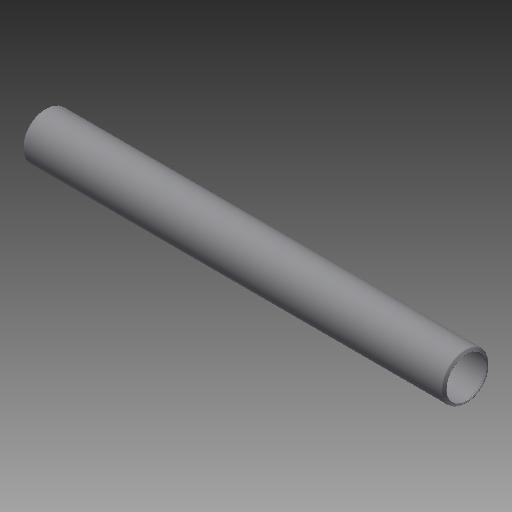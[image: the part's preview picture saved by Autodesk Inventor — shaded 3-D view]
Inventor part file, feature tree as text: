
AUTODESK INVENTOR PART (.ipt)
format: ipt  version: 2019 (Build 230136000, 136)  size: 144,384 bytes
history: native  units: in
note: dims shown in document units (in); Inventor stores cm internally (conversion verified against a paired STEP export)
features: other x42, revolve x1, sketch x1
ambient origin geometry x8: Origin, YZ Plane, XZ Plane, XY Plane, X Axis, Y Axis, Z Axis, Center Point
bodies: Solid1 (feature_tree)
feature tree (44):
  revolve  "Revolution1"  [1 undecoded]
  other  "cp1_XY"
  other  "cp1_YZ"
  other  "cp1_ZX"
  other  "cp1_X"
  other  "cp1_Y"
  other  "cp1_Z"
  other  "cp1_Center"
  other  "cp2_XY"
  other  "cp2_YZ"
  other  "cp2_ZX"
  other  "cp2_X"
  other  "cp2_Y"
  other  "cp2_Z"
  other  "cp2_Center"
  other  "cp3_XY"
  other  "cp3_YZ"
  other  "cp3_ZX"
  other  "cp3_X"
  other  "cp3_Y"
  other  "cp3_Z"
  other  "cp3_Center"
  other  "cp4_XY"
  other  "cp4_YZ"
  other  "cp4_ZX"
  other  "cp4_X"
  other  "cp4_Y"
  other  "cp4_Z"
  other  "cp4_Center"
  other  "tube_front_XY"
  other  "tube_front_YZ"
  other  "tube_front_ZX"
  other  "tube_front_X"
  other  "tube_front_Y"
  other  "tube_front_Z"
  other  "tube_front_Center"
  other  "tube_rear_XY"
  other  "tube_rear_YZ"
  other  "tube_rear_ZX"
  other  "tube_rear_X"
  other  "tube_rear_Y"
  other  "tube_rear_Z"
  other  "tube_rear_Center"
  sketch  "Sketch_1"  dims[d0=360.0deg]
note: 1 required parameter value undecoded (feature->parameter linkage not recoverable at this tier; creation-order binding heuristic only, values carry confidence <= 0.55)
